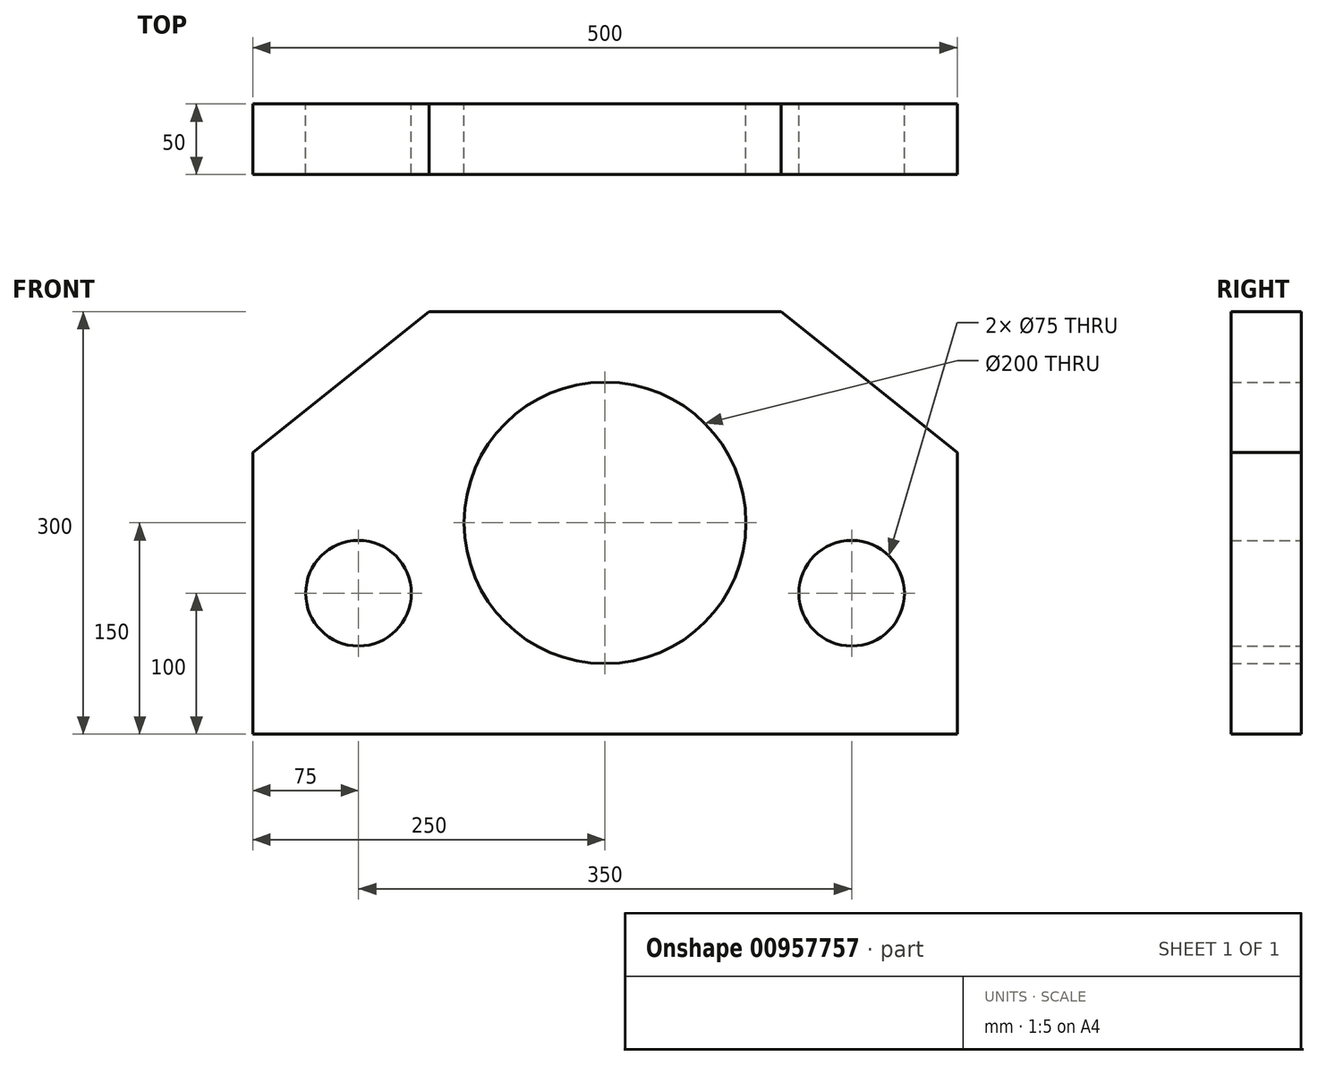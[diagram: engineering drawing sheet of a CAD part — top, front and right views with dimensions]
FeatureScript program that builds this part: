
annotation { "Feature Type Name" : "Feature", "Feature Type Description" : "" }
export const myFeature = defineFeature(function(context is Context, id is Id, definition is map)
    precondition{}
    {
        {
            var Q0;
            Q0=qCreatedBy(makeId("Front.planeOp"),FACE);
            var sketch = newSketch(context, id + "F0", { "sketchPlane" : qUnion([Q0])});
            skLineSegment(sketch, "E0.bottom", {"start": v(250, 150) * mm, "end": v(-250, 150) * mm});
            skLineSegment(sketch, "E0.top", {"start": v(250, -150) * mm, "end": v(-250, -150) * mm});
            skLineSegment(sketch, "E0.left", {"start": v(250, 150) * mm, "end": v(250, -150) * mm});
            skLineSegment(sketch, "E0.right", {"start": v(-250, 150) * mm, "end": v(-250, -150) * mm});
            skPoint(sketch, "E0.middle", {"position": v(0, 0) * mm});
            skLineSegment(sketch, "E1", {"start": v(-250, -150) * mm, "end": v(-250, 0) * mm});
            skLineSegment(sketch, "E2", {"start": v(-250, 0) * mm, "end": v(250, 0) * mm, "construction": true});
            skLineSegment(sketch, "E3", {"start": v(250, -150) * mm, "end": v(0, -150) * mm});
            skLineSegment(sketch, "E4", {"start": v(0, -150) * mm, "end": v(0, 150) * mm, "construction": true});
            skCircle(sketch, "E5", {"center": v(0, 0) * mm, "radius": 100 * mm});
            skCircle(sketch, "E6", {"center": v(175, -50) * mm, "radius": 37.5 * mm});
            skLineSegment(sketch, "E7", {"start": v(250, -150) * mm, "end": v(250, -50) * mm});
            skLineSegment(sketch, "E8", {"start": v(250, -150) * mm, "end": v(175, -150) * mm});
            skLineSegment(sketch, "E9", {"start": v(175, -150) * mm, "end": v(175, 150) * mm, "construction": true});
            skLineSegment(sketch, "E10", {"start": v(250, -50) * mm, "end": v(-250, -50) * mm, "construction": true});
            skLineSegment(sketch, "E11", {"start": v(250, 150) * mm, "end": v(250, 50) * mm});
            skLineSegment(sketch, "E12", {"start": v(250, 150) * mm, "end": v(125, 150) * mm});
            skLineSegment(sketch, "E13", {"start": v(125, 150) * mm, "end": v(250, 50) * mm});
            skLineSegment(sketch, "E14.MirrorCS", {"start": v(-125, 150) * mm, "end": v(-250, 50) * mm});
            skCircle(sketch, "E15.MirrorC", {"center": v(-175, -50) * mm, "radius": 37.5 * mm});
            skSolve(sketch);
        }
        {
            var Q0;
            Q0=makeQuery(id+"F0.imprint","IMPRINT",FACE,{"disambiguationData":[TD([[makeQuery(id+"F0.imprint","IMPRINT",EDGE,{"derivedFrom":sQuery(id+"F0.wireOp",EDGE,"E0.top")}),-1.0]])]});
            extrude(context, id + "F1", {"entities" : qUnion([Q0]), "depth" : 50 * mm, "offsetDistance" : 25 * mm});
        }
    });
